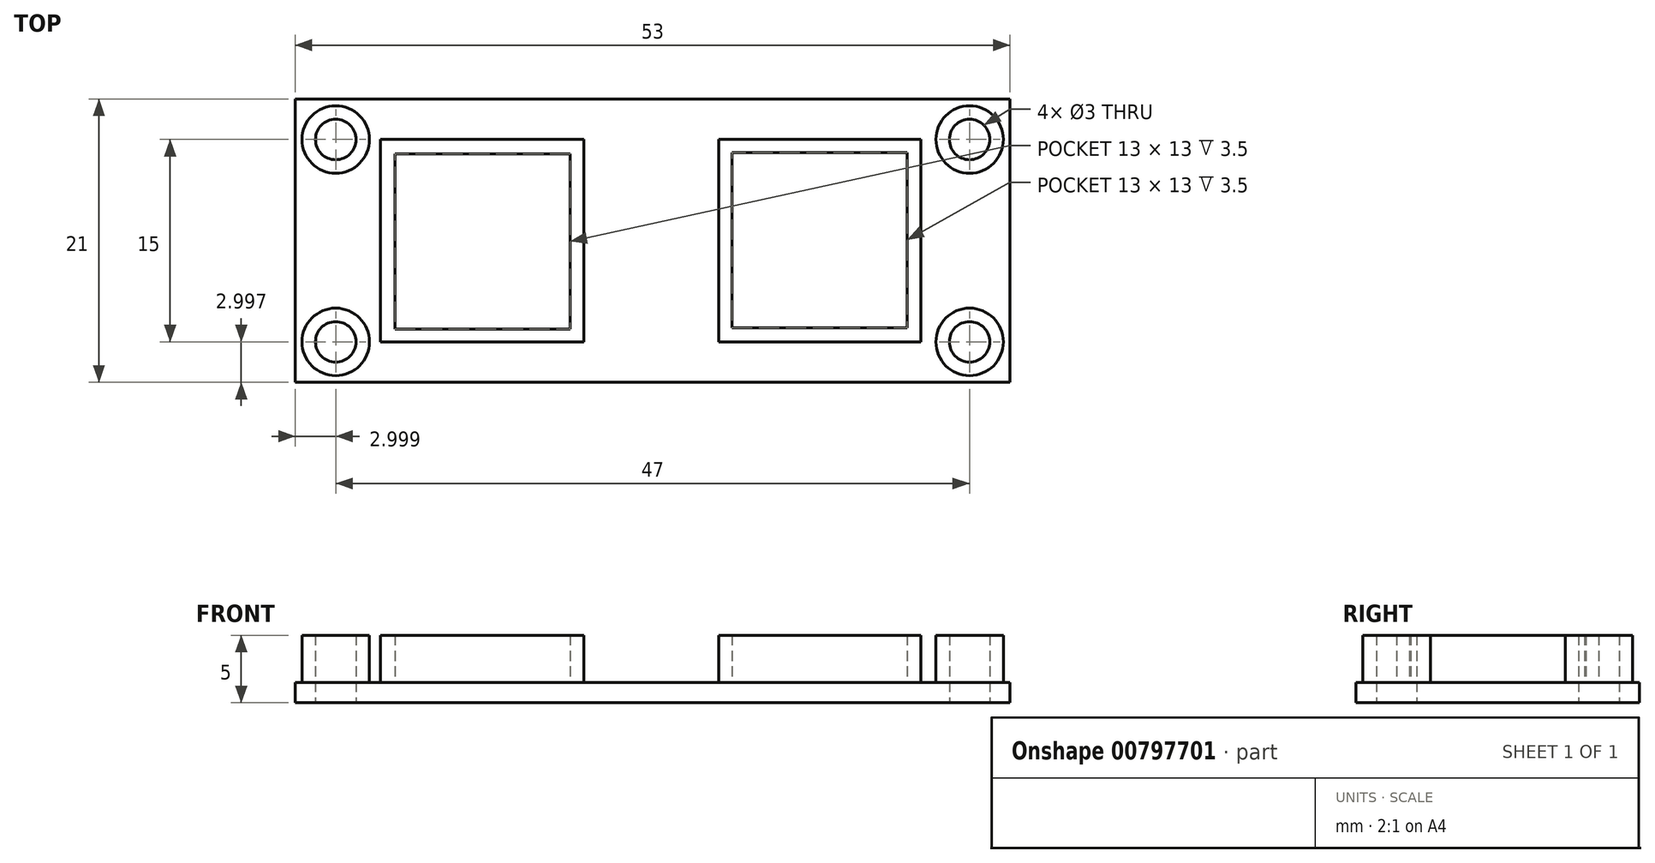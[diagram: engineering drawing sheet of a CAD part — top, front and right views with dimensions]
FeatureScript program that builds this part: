
annotation { "Feature Type Name" : "Feature", "Feature Type Description" : "" }
export const myFeature = defineFeature(function(context is Context, id is Id, definition is map)
    precondition{}
    {
        {
            var Q0;
            Q0=qCreatedBy(makeId("Top.planeOp"),FACE);
            var sketch = newSketch(context, id + "F0", { "sketchPlane" : qUnion([Q0])});
            skLineSegment(sketch, "E0.top", {"start": v(-26.38, -10.67) * mm, "end": v(26.62, -10.67) * mm});
            skLineSegment(sketch, "E0.left", {"start": v(-26.38, 10.33) * mm, "end": v(-26.38, -10.67) * mm});
            skLineSegment(sketch, "E0.right", {"start": v(26.62, 10.33) * mm, "end": v(26.62, -10.67) * mm});
            skLineSegment(sketch, "E1", {"start": v(26.62, 7.33) * mm, "end": v(-26.38, 7.33) * mm, "construction": true});
            skLineSegment(sketch, "E2", {"start": v(-26.38, -7.67) * mm, "end": v(26.62, -7.67) * mm, "construction": true});
            skLineSegment(sketch, "E3", {"start": v(23.62, 10.33) * mm, "end": v(23.62, -10.67) * mm, "construction": true});
            skLineSegment(sketch, "E4", {"start": v(-23.38, 10.33) * mm, "end": v(-23.38, -10.67) * mm, "construction": true});
            skCircle(sketch, "E5", {"center": v(-23.38, 7.33) * mm, "radius": 1.5 * mm});
            skCircle(sketch, "E6", {"center": v(-23.38, -7.67) * mm, "radius": 1.5 * mm});
            skCircle(sketch, "E7", {"center": v(23.62, 7.33) * mm, "radius": 1.5 * mm});
            skCircle(sketch, "E8", {"center": v(23.62, -7.67) * mm, "radius": 1.5 * mm});
            skLineSegment(sketch, "E9.bottom", {"start": v(-19, 6.27) * mm, "end": v(-6, 6.27) * mm});
            skLineSegment(sketch, "E9.top", {"start": v(-19, -6.73) * mm, "end": v(-6, -6.73) * mm});
            skLineSegment(sketch, "E9.left", {"start": v(-19, 6.27) * mm, "end": v(-19, -6.73) * mm});
            skLineSegment(sketch, "E9.right", {"start": v(-6, 6.27) * mm, "end": v(-6, -6.73) * mm});
            skLineSegment(sketch, "E10.bottom", {"start": v(6, 6.37) * mm, "end": v(19, 6.37) * mm});
            skLineSegment(sketch, "E10.top", {"start": v(6, -6.63) * mm, "end": v(19, -6.63) * mm});
            skLineSegment(sketch, "E10.left", {"start": v(6, 6.37) * mm, "end": v(6, -6.63) * mm});
            skLineSegment(sketch, "E10.right", {"start": v(19, 6.37) * mm, "end": v(19, -6.63) * mm});
            skLineSegment(sketch, "E11.bottom", {"start": v(-4.98, -7.67) * mm, "end": v(-20.06, -7.67) * mm});
            skLineSegment(sketch, "E11.top", {"start": v(-4.98, 7.33) * mm, "end": v(-20.06, 7.33) * mm});
            skLineSegment(sketch, "E11.left", {"start": v(-4.98, -7.67) * mm, "end": v(-4.98, 7.33) * mm});
            skLineSegment(sketch, "E11.right", {"start": v(-20.06, -7.67) * mm, "end": v(-20.06, 7.33) * mm});
            skLineSegment(sketch, "E12.bottom", {"start": v(5.01, 7.33) * mm, "end": v(20, 7.33) * mm});
            skLineSegment(sketch, "E12.top", {"start": v(5.01, -7.67) * mm, "end": v(20, -7.67) * mm});
            skLineSegment(sketch, "E12.left", {"start": v(5.01, 7.33) * mm, "end": v(5.01, -7.67) * mm});
            skLineSegment(sketch, "E12.right", {"start": v(20, 7.33) * mm, "end": v(20, -7.67) * mm});
            skLineSegment(sketch, "E13", {"start": v(-26.38, 10.33) * mm, "end": v(26.62, 10.33) * mm});
            skCircle(sketch, "E14", {"center": v(-23.38, 7.33) * mm, "radius": 2.5 * mm});
            skCircle(sketch, "E15", {"center": v(-23.38, -7.67) * mm, "radius": 2.5 * mm});
            skCircle(sketch, "E16", {"center": v(23.62, -7.67) * mm, "radius": 2.5 * mm});
            skCircle(sketch, "E17", {"center": v(23.62, 7.33) * mm, "radius": 2.5 * mm});
            skSolve(sketch);
        }
        {
            var Q0;
            Q0=makeQuery(id+"F0.imprint","IMPRINT",FACE,{"disambiguationData":[TD([[makeQuery(id+"F0.imprint","IMPRINT",EDGE,{"derivedFrom":sQuery(id+"F0.wireOp",EDGE,"E0.top")}),1.0]])]});
            var Q1;
            Q1=makeQuery(id+"F0.imprint","IMPRINT",FACE,{"disambiguationData":[TD([[makeQuery(id+"F0.imprint","IMPRINT",EDGE,{"derivedFrom":sQuery(id+"F0.wireOp",EDGE,"E9.bottom")}),1.0]])]});
            var Q2;
            Q2=makeQuery(id+"F0.imprint","IMPRINT",FACE,{"disambiguationData":[TD([[makeQuery(id+"F0.imprint","IMPRINT",EDGE,{"derivedFrom":sQuery(id+"F0.wireOp",EDGE,"E9.bottom")}),-1.0]])]});
            var Q3;
            Q3=makeQuery(id+"F0.imprint","IMPRINT",FACE,{"disambiguationData":[TD([[makeQuery(id+"F0.imprint","IMPRINT",EDGE,{"derivedFrom":sQuery(id+"F0.wireOp",EDGE,"E10.bottom")}),1.0]])]});
            var Q4;
            Q4=makeQuery(id+"F0.imprint","IMPRINT",FACE,{"disambiguationData":[TD([[makeQuery(id+"F0.imprint","IMPRINT",EDGE,{"derivedFrom":sQuery(id+"F0.wireOp",EDGE,"E10.bottom")}),-1.0]])]});
            extrude(context, id + "F1", {"entities" : qUnion([Q0, Q1, Q2, Q3, Q4]), "depth" : 1.5 * mm, "offsetDistance" : 25 * mm});
        }
        {
            var Q0;
            Q0=makeQuery(id+"F0.imprint","IMPRINT",FACE,{"disambiguationData":[TD([[makeQuery(id+"F0.imprint","IMPRINT",EDGE,{"derivedFrom":sQuery(id+"F0.wireOp",EDGE,"E9.bottom")}),1.0]])]});
            var Q1;
            Q1=makeQuery(id+"F0.imprint","IMPRINT",FACE,{"disambiguationData":[TD([[makeQuery(id+"F0.imprint","IMPRINT",EDGE,{"derivedFrom":sQuery(id+"F0.wireOp",EDGE,"E10.bottom")}),1.0]])]});
            extrude(context, id + "F2", {"entities" : qUnion([Q0, Q1]), "operationType" : NewBodyOperationType.ADD, "depth" : 5 * mm, "offsetDistance" : 25 * mm});
        }
        {
            var Q0;
            Q0=makeQuery(id+"F0.imprint","IMPRINT",FACE,{"disambiguationData":[TD([[makeQuery(id+"F0.imprint","IMPRINT",EDGE,{"derivedFrom":sQuery(id+"F0.wireOp",EDGE,"E5")}),-1.0]])]});
            var Q1;
            Q1=makeQuery(id+"F0.imprint","IMPRINT",FACE,{"disambiguationData":[TD([[makeQuery(id+"F0.imprint","IMPRINT",EDGE,{"derivedFrom":sQuery(id+"F0.wireOp",EDGE,"E6")}),-1.0]])]});
            var Q2;
            Q2=makeQuery(id+"F0.imprint","IMPRINT",FACE,{"disambiguationData":[TD([[makeQuery(id+"F0.imprint","IMPRINT",EDGE,{"derivedFrom":sQuery(id+"F0.wireOp",EDGE,"E8")}),-1.0]])]});
            var Q3;
            Q3=makeQuery(id+"F0.imprint","IMPRINT",FACE,{"disambiguationData":[TD([[makeQuery(id+"F0.imprint","IMPRINT",EDGE,{"derivedFrom":sQuery(id+"F0.wireOp",EDGE,"E7")}),-1.0]])]});
            extrude(context, id + "F3", {"entities" : qUnion([Q0, Q1, Q2, Q3]), "operationType" : NewBodyOperationType.ADD, "depth" : 5 * mm, "offsetDistance" : 25 * mm});
        }
    });
